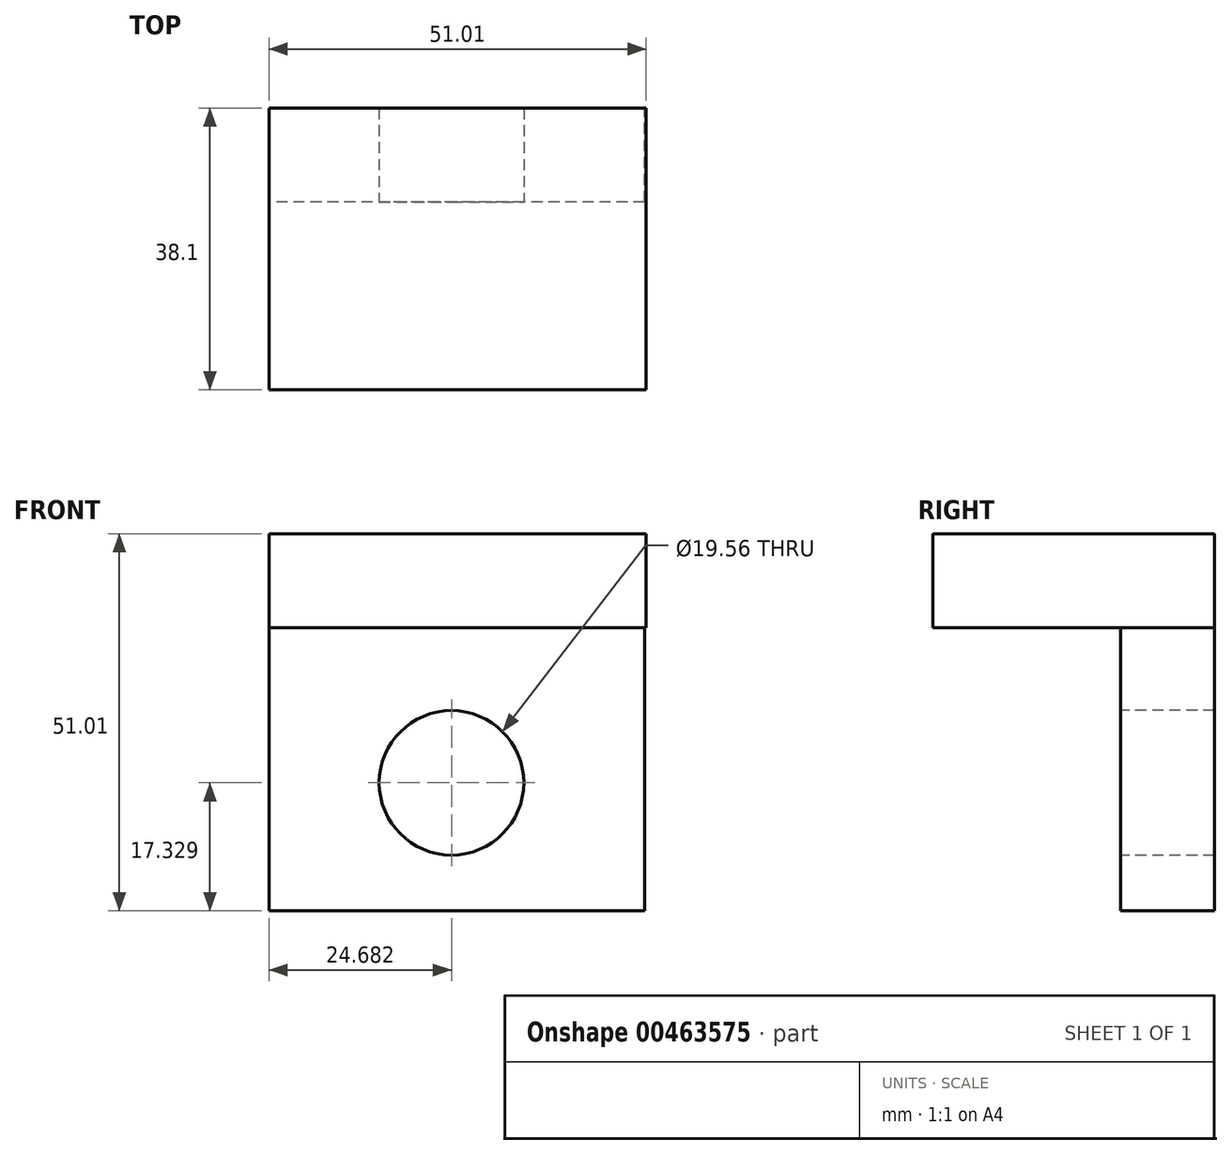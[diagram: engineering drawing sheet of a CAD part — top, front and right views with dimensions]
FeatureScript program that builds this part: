
annotation { "Feature Type Name" : "Feature", "Feature Type Description" : "" }
export const myFeature = defineFeature(function(context is Context, id is Id, definition is map)
    precondition{}
    {
        {
            var Q0;
            Q0=qCreatedBy(makeId("Front.planeOp"),FACE);
            var sketch = newSketch(context, id + "F0", { "sketchPlane" : qUnion([Q0])});
            skLineSegment(sketch, "E0.bottom", {"start": v(0, 0) * mm, "end": v(50.8, 0) * mm});
            skLineSegment(sketch, "E0.top", {"start": v(0, 50.8) * mm, "end": v(50.8, 50.8) * mm});
            skLineSegment(sketch, "E0.left", {"start": v(0, 0) * mm, "end": v(0, 50.8) * mm});
            skLineSegment(sketch, "E0.right", {"start": v(50.8, 0) * mm, "end": v(50.8, 50.8) * mm});
            skSolve(sketch);
        }
        {
            var Q0;
            Q0=makeQuery(id+"F0.imprint","IMPRINT",FACE,{"disambiguationData":[TD([[makeQuery(id+"F0.imprint","IMPRINT",EDGE,{"derivedFrom":sQuery(id+"F0.wireOp",EDGE,"E0.bottom")}),1.0]])]});
            extrude(context, id + "F1", {"entities" : qUnion([Q0]), "depth" : 12.7 * mm});
        }
        {
            var Q0;
            Q0=qCreatedBy(makeId("Front.planeOp"),FACE);
            var sketch = newSketch(context, id + "F2", { "sketchPlane" : qUnion([Q0])});
            skPoint(sketch, "E1", {"position": v(0, 51) * mm});
            skPoint(sketch, "E2", {"position": v(50.5, 51) * mm});
            skLineSegment(sketch, "E3.bottom", {"start": v(0, 51) * mm, "end": v(51, 51) * mm});
            skLineSegment(sketch, "E3.top", {"start": v(0, 38.32) * mm, "end": v(51, 38.32) * mm});
            skLineSegment(sketch, "E3.left", {"start": v(0, 51) * mm, "end": v(0, 38.32) * mm});
            skLineSegment(sketch, "E3.right", {"start": v(51, 51) * mm, "end": v(51, 38.32) * mm});
            skSolve(sketch);
        }
        {
            var Q0;
            Q0 = qSketchRegion(id + "F2", true);
            extrude(context, id + "F3", {"entities" : qUnion([Q0]), "operationType" : NewBodyOperationType.ADD, "depth" : 38.1 * mm});
        }
        {
            var Q0;
            Q0=makeQuery(id+"F1.opExtrude","CAP_FACE",FACE,{"disambiguationData":[OSD([sQuery(id+"F0.wireOp",EDGE,"E0.bottom"),sQuery(id+"F0.wireOp",EDGE,"E0.top"),sQuery(id+"F0.wireOp",EDGE,"E0.left"),sQuery(id+"F0.wireOp",EDGE,"E0.right")])],"isStart":false});
            var sketch = newSketch(context, id + "F4", { "sketchPlane" : qUnion([Q0])});
            skCircle(sketch, "E4", {"center": v(24.68, 17.33) * mm, "radius": 9.78 * mm});
            skSolve(sketch);
        }
        {
            var Q0;
            Q0=makeQuery(id+"F4.imprint","IMPRINT",FACE,{"disambiguationData":[TD([[makeQuery(id+"F4.imprint","IMPRINT",EDGE,{"derivedFrom":sQuery(id+"F4.wireOp",EDGE,"E4")}),1.0]])]});
            extrude(context, id + "F5", {"entities" : qUnion([Q0]), "operationType" : NewBodyOperationType.REMOVE, "endBound" : BoundingType.UP_TO_NEXT, "oppositeDirection" : true, "depth" : 12.7 * mm});
        }
    });
